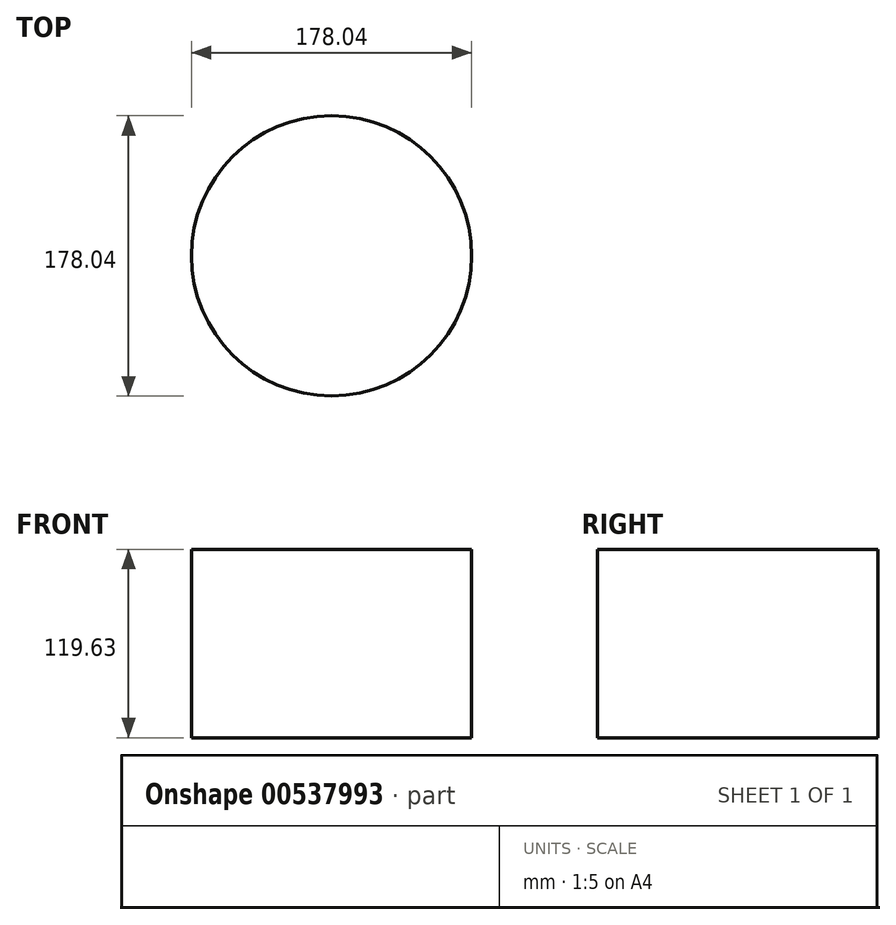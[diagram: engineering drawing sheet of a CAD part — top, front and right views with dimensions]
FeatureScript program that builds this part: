
annotation { "Feature Type Name" : "Feature", "Feature Type Description" : "" }
export const myFeature = defineFeature(function(context is Context, id is Id, definition is map)
    precondition{}
    {
        {
            var Q0;
            Q0=qCreatedBy(makeId("Top.planeOp"),FACE);
            var sketch = newSketch(context, id + "F0", { "sketchPlane" : qUnion([Q0])});
            skCircle(sketch, "E0", {"center": v(0, 0) * mm, "radius": 89.02 * mm});
            skCircle(sketch, "E1", {"center": v(0, 5.85) * mm, "radius": 72.87 * mm});
            skSolve(sketch);
        }
        {
            var Q0;
            Q0=makeQuery(id+"F0.imprint","IMPRINT",FACE,{"disambiguationData":[TD([[makeQuery(id+"F0.imprint","IMPRINT",EDGE,{"derivedFrom":sQuery(id+"F0.wireOp",EDGE,"E0")}),1.0]])]});
            var Q1;
            Q1=makeQuery(id+"F0.imprint","IMPRINT",FACE,{"disambiguationData":[TD([[makeQuery(id+"F0.imprint","IMPRINT",EDGE,{"derivedFrom":sQuery(id+"F0.wireOp",EDGE,"E1")}),1.0]])]});
            extrude(context, id + "F1", {"entities" : qUnion([Q0, Q1]), "depth" : 119.63 * mm, "offsetDistance" : 25.4 * mm});
        }
    });
